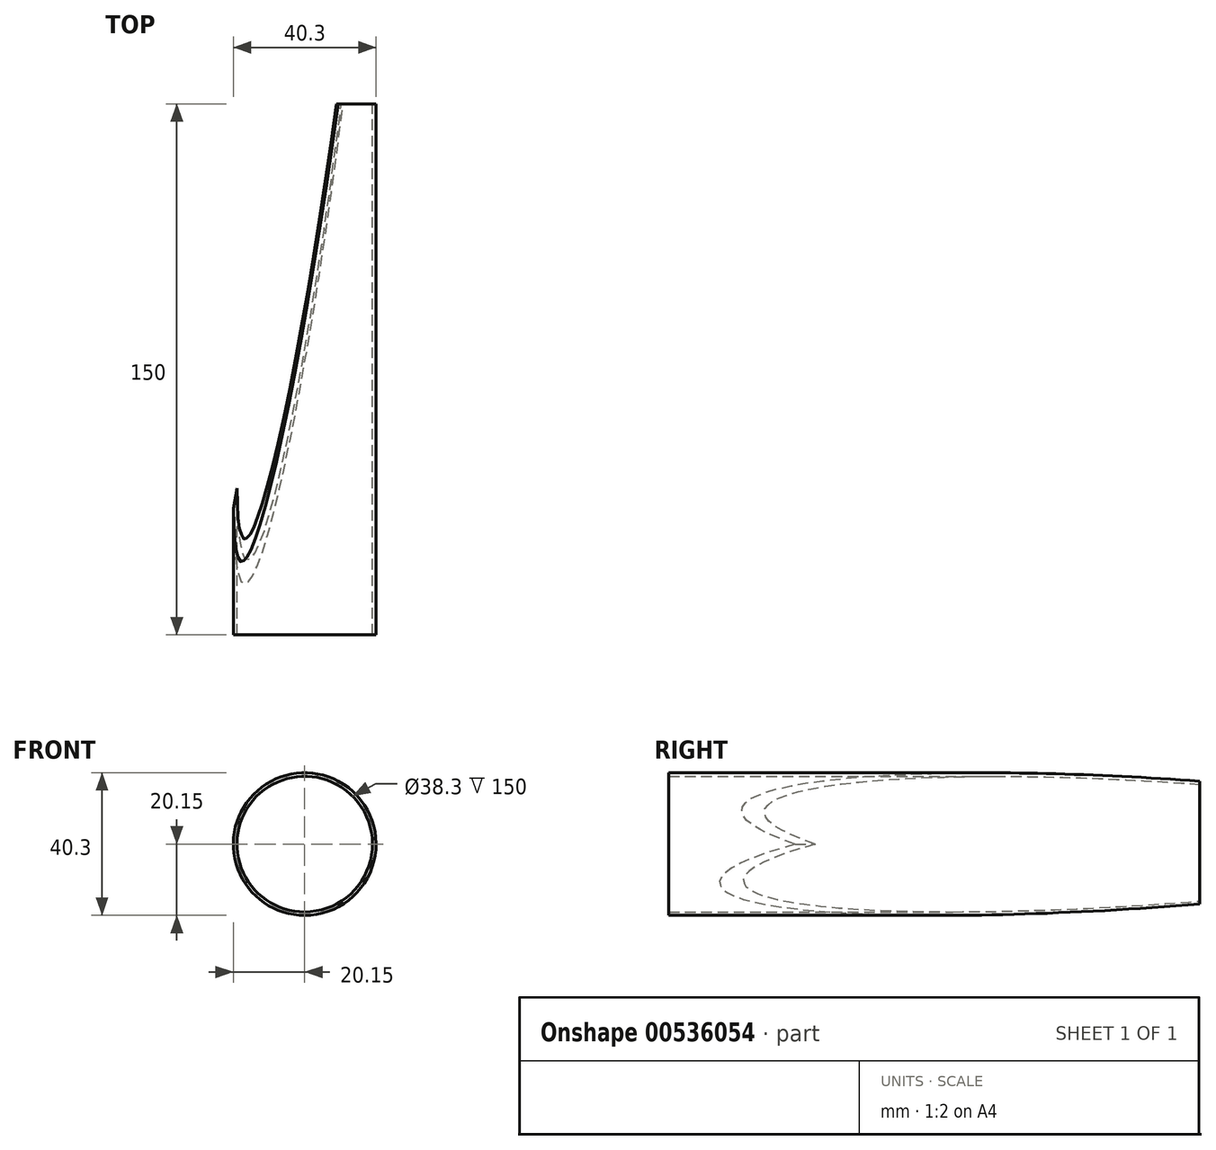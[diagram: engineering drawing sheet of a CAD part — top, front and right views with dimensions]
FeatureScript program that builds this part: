
annotation { "Feature Type Name" : "Feature", "Feature Type Description" : "" }
export const myFeature = defineFeature(function(context is Context, id is Id, definition is map)
    precondition{}
    {
        {
            var Q0;
            Q0=qCreatedBy(makeId("Front.planeOp"),FACE);
            var sketch = newSketch(context, id + "F0", { "sketchPlane" : qUnion([Q0])});
            skCircle(sketch, "E0", {"center": v(0, 0) * mm, "radius": 19.15 * mm});
            skCircle(sketch, "E1", {"center": v(0, 0) * mm, "radius": 20.15 * mm});
            skLineSegment(sketch, "E2", {"start": v(0, 12.16) * mm, "end": v(0, -11.63) * mm});
            skSolve(sketch);
        }
        {
            var Q0;
            Q0=makeQuery(id+"F0.imprint","IMPRINT",FACE,{"disambiguationData":[TD([[makeQuery(id+"F0.imprint","IMPRINT",EDGE,{"derivedFrom":sQuery(id+"F0.wireOp",EDGE,"E0")}),-1.0]])]});
            extrude(context, id + "F1", {"entities" : qUnion([Q0]), "depth" : 150 * mm, "offsetDistance" : 25 * mm});
        }
        {
            var Q0;
            Q0=sQuery(id+"F0.wireOp",EDGE,"E2");
            var Q1;
            Q1=qCreatedBy(makeId("Front.planeOp"),FACE);
            cPlane(context, id + "F2", {"entities" : qUnion([Q0, Q1]), "cplaneType" : CPlaneType.LINE_ANGLE, "offset" : 25 * mm, "angle" : 10 * degree, "width" : 150 * mm, "height" : 150 * mm});
        }
        {
            var Q0;
            Q0=qCreatedBy(id+"F2.planeOp",FACE);
            var sketch = newSketch(context, id + "F3", { "sketchPlane" : qUnion([Q0])});
            skArc(sketch, "E3", {"start": v(-16.03, -25.36) * mm, "mid": v(29.98, -1.2) * mm, "end": v(-13.95, 26.56) * mm});
            skLineSegment(sketch, "E4", {"start": v(0, 0) * mm, "end": v(-13.95, 26.56) * mm});
            skLineSegment(sketch, "E5", {"start": v(0, 0) * mm, "end": v(-16.03, -25.36) * mm});
            skSolve(sketch);
        }
        {
            var Q0;
            Q0=makeQuery(id+"F3.imprint","IMPRINT",FACE,{"disambiguationData":[TD([[makeQuery(id+"F3.imprint","IMPRINT",EDGE,{"derivedFrom":sQuery(id+"F3.wireOp",EDGE,"E3")}),1.0]])]});
            extrude(context, id + "F4", {"entities" : qUnion([Q0]), "operationType" : NewBodyOperationType.REMOVE, "endBound" : BoundingType.THROUGH_ALL, "oppositeDirection" : true, "depth" : 25 * mm, "offsetDistance" : 25 * mm});
        }
        {
            var Q0;
            Q0=makeQuery(id+"F3.imprint","IMPRINT",FACE,{"disambiguationData":[TD([[makeQuery(id+"F3.imprint","IMPRINT",EDGE,{"derivedFrom":sQuery(id+"F3.wireOp",EDGE,"E3")}),1.0]])]});
            extrude(context, id + "F5", {"entities" : qUnion([Q0]), "operationType" : NewBodyOperationType.REMOVE, "endBound" : BoundingType.THROUGH_ALL, "depth" : 25 * mm, "offsetDistance" : 25 * mm});
        }
    });
